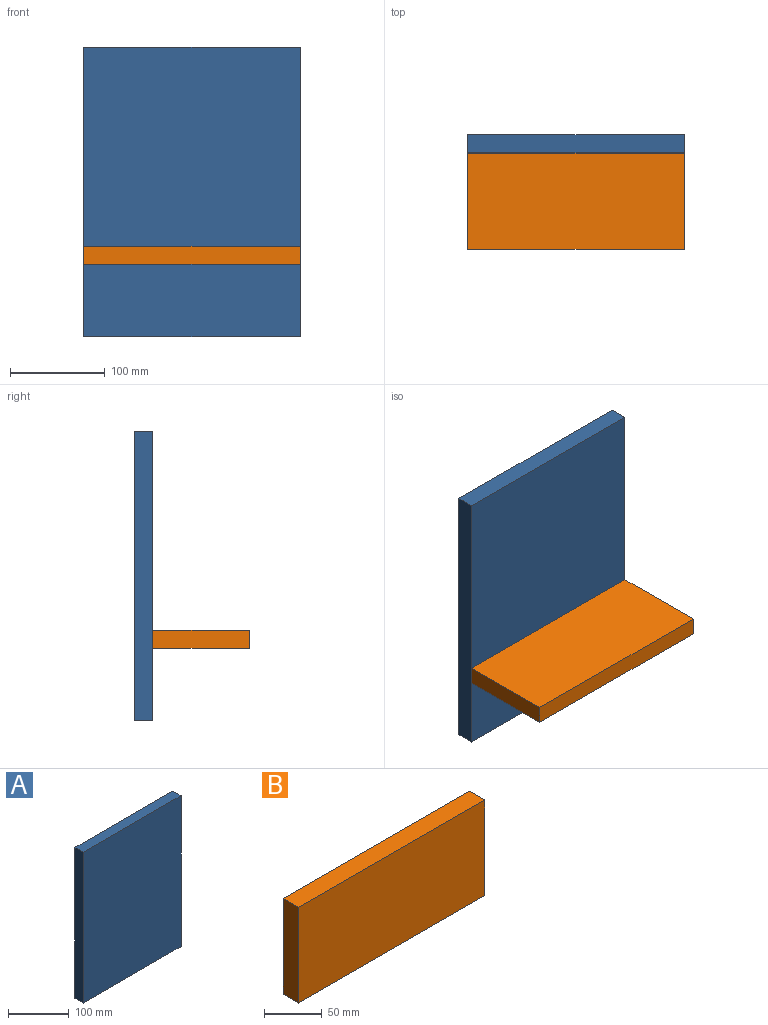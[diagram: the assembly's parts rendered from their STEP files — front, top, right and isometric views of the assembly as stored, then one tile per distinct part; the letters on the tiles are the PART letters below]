
ASSEMBLY  parts=2 mates=1
PART A: 6 faces, bbox 228.6x19.1x304.8 mm
  f0: plane 304.8x19.05mm, normal (-1,0,0), area 5806.4mm2, adj f1,f3,f4,f5
  f1: plane 304.8x228.6mm, normal (0,-1,0), area 69677.3mm2, adj f0,f2,f4,f5
  f2: plane 304.8x19.05mm, normal (1,0,0), area 5806.4mm2, adj f1,f3,f4,f5
  f3: plane 304.8x228.6mm, normal (0,1,0), area 69677.3mm2, adj f0,f2,f4,f5
  f4: plane 228.6x19.05mm, normal (0,0,1), area 4354.8mm2, adj f0,f1,f2,f3
  f5: plane 228.6x19.05mm, normal (0,0,-1), area 4354.8mm2, adj f0,f1,f2,f3
PART B: 6 faces, bbox 228.6x19.1x101.6 mm
  f0: plane 101.6x19.05mm, normal (-1,0,0), area 1935.5mm2, adj f1,f3,f4,f5
  f1: plane 228.6x101.6mm, normal (0,-1,0), area 23225.8mm2, adj f0,f2,f4,f5
  f2: plane 101.6x19.05mm, normal (1,0,0), area 1935.5mm2, adj f1,f3,f4,f5
  f3: plane 228.6x101.6mm, normal (0,1,0), area 23225.8mm2, adj f0,f2,f4,f5
  f4: plane 228.6x19.05mm, normal (0,0,1), area 4354.8mm2, adj f0,f1,f2,f3
  f5: plane 228.6x19.05mm, normal (0,0,-1), area 4354.8mm2, adj f0,f1,f2,f3
PLACE A at identity
PLACE B rot(axis=(-1,0,0),90deg) t=(0,-101.6,95.25)mm
MATE fastened B.f4 <-> A.f1  axis (0,1,0) through (228.6,0,76.2)mm
